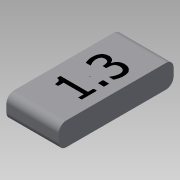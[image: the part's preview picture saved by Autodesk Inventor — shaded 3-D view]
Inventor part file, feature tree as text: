
AUTODESK INVENTOR PART (.ipt)
format: ipt  version: 2015 SP1 (Build 190203100, 203)  size: 82,944 bytes
history: native  units: mm
features: sketch x2, extrude x1, fillet x1
ambient origin geometry x8: Origin, YZ Plane, XZ Plane, XY Plane, X Axis, Y Axis, Z Axis, Center Point
bodies: Solid1 (feature_tree)
feature tree (4):
  extrude  "Extrusion1"  Depth=74.83mm
  fillet  "Fillet1"  Radius=15.09mm
  sketch  "Sketch2"  dims[d4=5.0mm]
  sketch  "Sketch1"  dims[d0=34.0mm d1=74.83mm d2=15.09mm d3=0.0mm]
